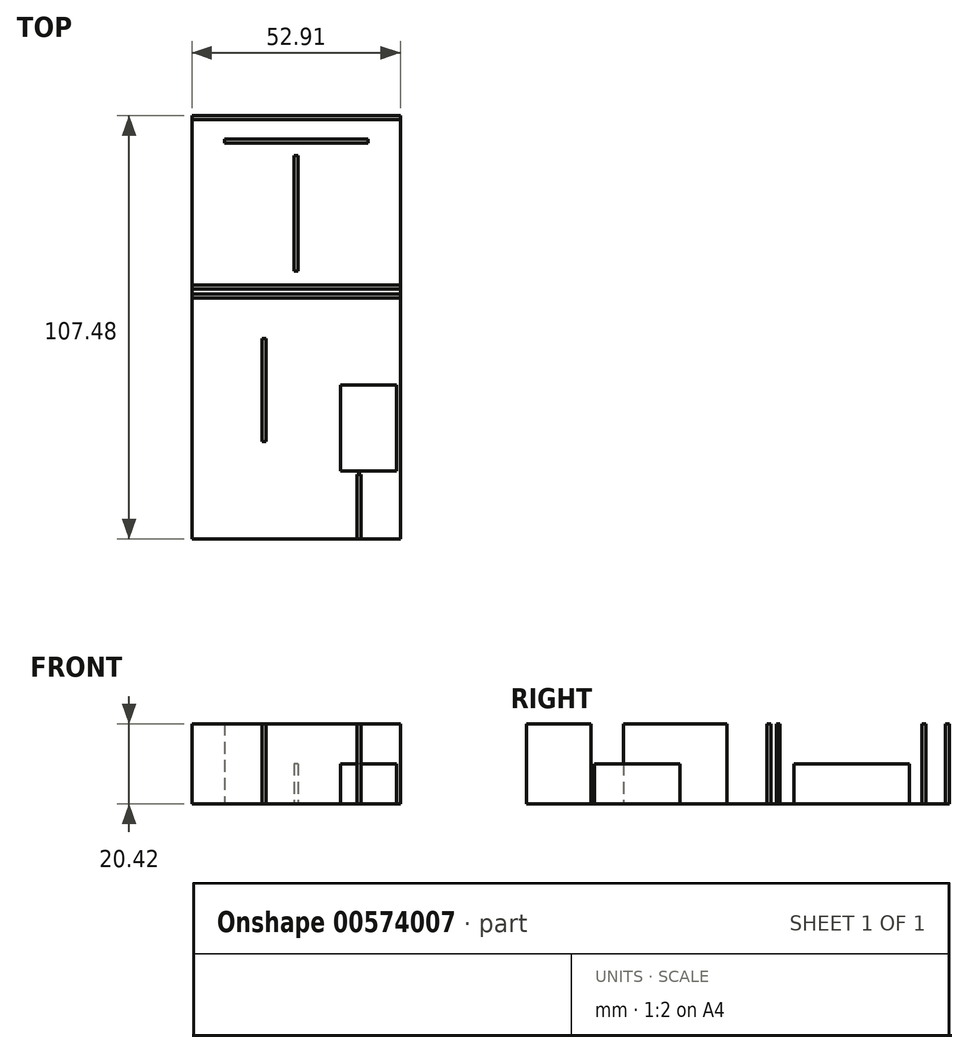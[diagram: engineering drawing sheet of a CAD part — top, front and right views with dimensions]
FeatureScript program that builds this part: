
annotation { "Feature Type Name" : "Feature", "Feature Type Description" : "" }
export const myFeature = defineFeature(function(context is Context, id is Id, definition is map)
    precondition{}
    {
        {
            var Q0;
            Q0=qCreatedBy(makeId("Top.planeOp"),FACE);
            var sketch = newSketch(context, id + "F0", { "sketchPlane" : qUnion([Q0])});
            skLineSegment(sketch, "E0.bottom", {"start": v(-37.8, 43.32) * mm, "end": v(15.12, 43.32) * mm});
            skLineSegment(sketch, "E0.top", {"start": v(-37.8, -64.16) * mm, "end": v(15.12, -64.16) * mm});
            skLineSegment(sketch, "E0.left", {"start": v(-37.8, 43.32) * mm, "end": v(-37.8, -64.16) * mm});
            skLineSegment(sketch, "E0.right", {"start": v(15.12, 43.32) * mm, "end": v(15.12, -64.16) * mm});
            skSolve(sketch);
        }
        {
            var Q0;
            Q0 = qSketchRegion(id + "F0", true);
            extrude(context, id + "F1", {"entities" : qUnion([Q0]), "depth" : .1 * mm, "offsetDistance" : 25.4 * mm});
        }
        {
            var Q0;
            Q0=makeQuery(id+"F1.opExtrude","CAP_FACE",FACE,{"disambiguationData":[OSD([sQuery(id+"F0.wireOp",EDGE,"E0.bottom"),sQuery(id+"F0.wireOp",EDGE,"E0.top"),sQuery(id+"F0.wireOp",EDGE,"E0.left"),sQuery(id+"F0.wireOp",EDGE,"E0.right")])],"isStart":false});
            var sketch = newSketch(context, id + "F2", { "sketchPlane" : qUnion([Q0])});
            skLineSegment(sketch, "E1.bottom", {"start": v(-29.53, 37.35) * mm, "end": v(6.85, 37.35) * mm});
            skLineSegment(sketch, "E1.top", {"start": v(-29.53, 36.35) * mm, "end": v(6.85, 36.35) * mm});
            skLineSegment(sketch, "E1.left", {"start": v(-29.53, 37.35) * mm, "end": v(-29.53, 36.35) * mm});
            skLineSegment(sketch, "E1.right", {"start": v(6.85, 37.35) * mm, "end": v(6.85, 36.35) * mm});
            skLineSegment(sketch, "E2.bottom", {"start": v(-10.84, 33.22) * mm, "end": v(-11.84, 33.22) * mm});
            skLineSegment(sketch, "E2.top", {"start": v(-10.84, 3.86) * mm, "end": v(-11.84, 3.86) * mm});
            skLineSegment(sketch, "E2.left", {"start": v(-10.84, 33.22) * mm, "end": v(-10.84, 3.86) * mm});
            skLineSegment(sketch, "E2.right", {"start": v(-11.84, 33.22) * mm, "end": v(-11.84, 3.86) * mm});
            skLineSegment(sketch, "E3.bottom", {"start": v(-37.8, -2) * mm, "end": v(15.12, -2) * mm});
            skLineSegment(sketch, "E4.top", {"start": v(-37.8, -3) * mm, "end": v(15.12, -3) * mm});
            skLineSegment(sketch, "E4.left", {"start": v(-37.8, -2) * mm, "end": v(-37.8, -3) * mm});
            skLineSegment(sketch, "E4.right", {"start": v(15.12, -2) * mm, "end": v(15.12, -3) * mm});
            skLineSegment(sketch, "E5.bottom", {"start": v(-18.97, -13.22) * mm, "end": v(-19.97, -13.22) * mm});
            skLineSegment(sketch, "E5.top", {"start": v(-18.97, -39.45) * mm, "end": v(-19.97, -39.45) * mm});
            skLineSegment(sketch, "E5.left", {"start": v(-18.97, -13.22) * mm, "end": v(-18.97, -39.45) * mm});
            skLineSegment(sketch, "E5.right", {"start": v(-19.97, -13.22) * mm, "end": v(-19.97, -39.45) * mm});
            skLineSegment(sketch, "E6.bottom", {"start": v(4.14, -47.77) * mm, "end": v(5.14, -47.77) * mm});
            skLineSegment(sketch, "E6.top", {"start": v(4.14, -64.16) * mm, "end": v(5.14, -64.16) * mm});
            skLineSegment(sketch, "E6.left", {"start": v(4.14, -47.77) * mm, "end": v(4.14, -64.16) * mm});
            skLineSegment(sketch, "E6.right", {"start": v(5.14, -47.77) * mm, "end": v(5.14, -64.16) * mm});
            skLineSegment(sketch, "E7.bottom", {"start": v(-37.8, 43.32) * mm, "end": v(15.12, 43.32) * mm});
            skLineSegment(sketch, "E7.top", {"start": v(-37.8, 42.32) * mm, "end": v(15.12, 42.32) * mm});
            skLineSegment(sketch, "E7.left", {"start": v(-37.8, 43.32) * mm, "end": v(-37.8, 42.32) * mm});
            skLineSegment(sketch, "E7.right", {"start": v(15.12, 43.32) * mm, "end": v(15.12, 42.32) * mm});
            skLineSegment(sketch, "E8", {"start": v(-11.34, 33.22) * mm, "end": v(-11.34, 36.35) * mm, "construction": true});
            skPoint(sketch, "E8.endSnap0", {"position": v(-11.34, 36.35) * mm});
            skLineSegment(sketch, "E9.bottom", {"start": v(-20.06, -3) * mm, "end": v(-2.62, -3) * mm});
            skLineSegment(sketch, "E9.top", {"start": v(-20.06, -12.1) * mm, "end": v(-2.62, -12.1) * mm});
            skLineSegment(sketch, "E9.left", {"start": v(-20.06, -3) * mm, "end": v(-20.06, -12.1) * mm});
            skLineSegment(sketch, "E9.right", {"start": v(-2.62, -3) * mm, "end": v(-2.62, -12.1) * mm});
            skLineSegment(sketch, "E10", {"start": v(-11.34, 3.86) * mm, "end": v(-11.34, -12.1) * mm, "construction": true});
            skLineSegment(sketch, "E11", {"start": v(6.85, 36.85) * mm, "end": v(15.12, 36.85) * mm, "construction": true});
            skLineSegment(sketch, "E12", {"start": v(-29.53, 36.85) * mm, "end": v(-37.8, 36.85) * mm, "construction": true});
            skLineSegment(sketch, "E13.bottom", {"start": v(14.14, -25.06) * mm, "end": v(-0.06, -25.06) * mm});
            skLineSegment(sketch, "E13.top", {"start": v(14.14, -46.88) * mm, "end": v(-0.06, -46.88) * mm});
            skLineSegment(sketch, "E13.left", {"start": v(14.14, -25.06) * mm, "end": v(14.14, -46.88) * mm});
            skLineSegment(sketch, "E13.right", {"start": v(-0.06, -25.06) * mm, "end": v(-0.06, -46.88) * mm});
            skLineSegment(sketch, "E14", {"start": v(14.14, -35.97) * mm, "end": v(-0.06, -35.97) * mm, "construction": true});
            skArc(sketch, "E15", {"start": v(-18.97, -13.22) * mm, "mid": v(-1.69, -19.71) * mm, "end": v(7.04, -35.97) * mm});
            skLineSegment(sketch, "E16.bottom", {"start": v(15.12, -0.67) * mm, "end": v(-37.8, -0.67) * mm});
            skLineSegment(sketch, "E16.top", {"start": v(15.12, 0.33) * mm, "end": v(-37.8, 0.33) * mm});
            skLineSegment(sketch, "E16.left", {"start": v(15.12, -0.67) * mm, "end": v(15.12, 0.33) * mm});
            skLineSegment(sketch, "E16.right", {"start": v(-37.8, -0.67) * mm, "end": v(-37.8, 0.33) * mm});
            skSolve(sketch);
        }
        {
            var Q0;
            Q0=makeQuery(id+"F2.imprint","IMPRINT",FACE,{"disambiguationData":[TD([[makeQuery(id+"F2.imprint","IMPRINT",EDGE,{"derivedFrom":sQuery(id+"F2.wireOp",EDGE,"E7.bottom")}),-1.0]])]});
            var Q1;
            Q1=makeQuery(id+"F2.imprint","IMPRINT",FACE,{"disambiguationData":[TD([[makeQuery(id+"F2.imprint","IMPRINT",EDGE,{"derivedFrom":sQuery(id+"F2.wireOp",EDGE,"E1.bottom")}),-1.0]])]});
            var Q2;
            Q2=makeQuery(id+"F2.imprint","IMPRINT",FACE,{"disambiguationData":[TD([[makeQuery(id+"F2.imprint","IMPRINT",EDGE,{"derivedFrom":sQuery(id+"F2.wireOp",EDGE,"E3.top")}),-1.0]])]});
            var Q3;
            Q3=makeQuery(id+"F2.imprint","IMPRINT",FACE,{"disambiguationData":[TD([[makeQuery(id+"F2.imprint","IMPRINT",EDGE,{"derivedFrom":sQuery(id+"F2.wireOp",EDGE,"E3.bottom")}),-1.0]])]});
            var Q4;
            Q4=makeQuery(id+"F2.imprint","IMPRINT",FACE,{"disambiguationData":[TD([[makeQuery(id+"F2.imprint","IMPRINT",EDGE,{"derivedFrom":sQuery(id+"F2.wireOp",EDGE,"E5.bottom")}),1.0]])]});
            var Q5;
            Q5=makeQuery(id+"F2.imprint","IMPRINT",FACE,{"disambiguationData":[TD([[makeQuery(id+"F2.imprint","IMPRINT",EDGE,{"derivedFrom":sQuery(id+"F2.wireOp",EDGE,"E6.bottom")}),-1.0]])]});
            var Q6;
            Q6=makeQuery(id+"F2.imprint","IMPRINT",FACE,{"disambiguationData":[TD([[makeQuery(id+"F2.imprint","IMPRINT",EDGE,{"derivedFrom":sQuery(id+"F2.wireOp",EDGE,"E16.bottom")}),-1.0]])]});
            extrude(context, id + "F3", {"entities" : qUnion([Q0, Q1, Q2, Q3, Q4, Q5, Q6]), "depth" : 20.32 * mm, "offsetDistance" : 25.4 * mm});
        }
        {
            var Q0;
            Q0=makeQuery(id+"F2.imprint","IMPRINT",FACE,{"disambiguationData":[TD([[makeQuery(id+"F2.imprint","IMPRINT",EDGE,{"derivedFrom":sQuery(id+"F2.wireOp",EDGE,"E2.bottom")}),1.0]])]});
            var Q1;
            Q1=makeQuery(id+"F2.imprint","IMPRINT",FACE,{"disambiguationData":[TD([[makeQuery(id+"F2.imprint","IMPRINT",EDGE,{"derivedFrom":sQuery(id+"F2.wireOp",EDGE,"E9.bottom")}),-1.0]])]});
            var Q2;
            Q2=makeQuery(id+"F2.imprint","IMPRINT",FACE,{"disambiguationData":[TD([[makeQuery(id+"F2.imprint","IMPRINT",EDGE,{"derivedFrom":sQuery(id+"F2.wireOp",EDGE,"E13.top")}),-1.0]])]});
            extrude(context, id + "F4", {"entities" : qUnion([Q0, Q1, Q2]), "depth" : 10.16 * mm, "offsetDistance" : 25.4 * mm});
        }
        {
            var Q0;
            Q0=sQuery(id+"F2.wireOp",EDGE,"E15");
            extrude(context, id + "F5", {"bodyType" : ToolBodyType.SURFACE, "surfaceEntities" : qUnion([Q0]), "depth" : 25.4 * mm, "offsetDistance" : 25.4 * mm});
        }
    });
